# Revit family: Toilet_Elongated-American_Standard-Champion_Pro-3195C101_Series
name_source: partatom
category: Plumbing Fixtures
units: mm (PartAtom-declared; Revit-internal decimal feet)

## family parameters
Always vertical = No
Cut with Voids When Loaded = No
OmniClass Number = 23.45.05.21.11.11
OmniClass Title = Water Operated Water Closets
Part Type = Normal
Room Calculation Point = No
Round Connector Dimension = Use Radius
Shared = Yes
Work Plane-Based = Yes

## types (1)
- 3195C101.020
    4225A.004 Tank = No
    4225A.005 Tank complete with trip lever = No
    4225A.064 Tank complete with tank cover = No
    ADA Compliant = Yes
    Assembly Code = D2010110
    Bowl Shape = Elongated
    CEC Compliant = Yes
    CW Connection = Yes
    CWFU = 10
    Cold Water Connection Diameter = 1/2"
    Cold Water Connection Height = 10"
    Cold Water Connection Radius = 1/4"
    Cold Water Connection Width = 6"
    Default Elevation = 0"
    Description = Champion® PRO Standard Height Elongated Bowl
    Finish = Vitreous China-American Standard-020-White
    Flush Rate = 1.6 gpf (6.0 Lpf)
    HW Connection = No
    HWFU = 0
    Height = 15"
    IAPMO Compliance = ASME A112.19.2-2008/CSA B45.1-08 for Vitreous China Fixtures, US EPA WaterSense® Specification for HETs
    Installation Type = Floor Mounted
    Length = 30 1/4"
    Manufacturer = American Standard
    Material = Vitreous China-American Standard-020-White
    Model = 3195C101.020
    Price = Prices may vary. Please consult Manufacturer Representative for most up-to-date price list.
    Product Documentation Link = https://americanstandard.box.com
    Product Page URL = https://www.americanstandard-us.com
    Seat 5325.010 Elongated Champion Slow Close = No
    URL = http://www.americanstandard-us.com
    Vent Connection = No
    WFU = 10
    Warranty Information = 10 Year Warranty
    Waste Connection = Yes
    Waste Connection Diameter = 2 3/8"
    Waste Connection Radius = 1 3/16"
    Width = 14"

## geometry (parser evidence)
native form markers: Sweep x4
no freeform markers — native parametric forms only
